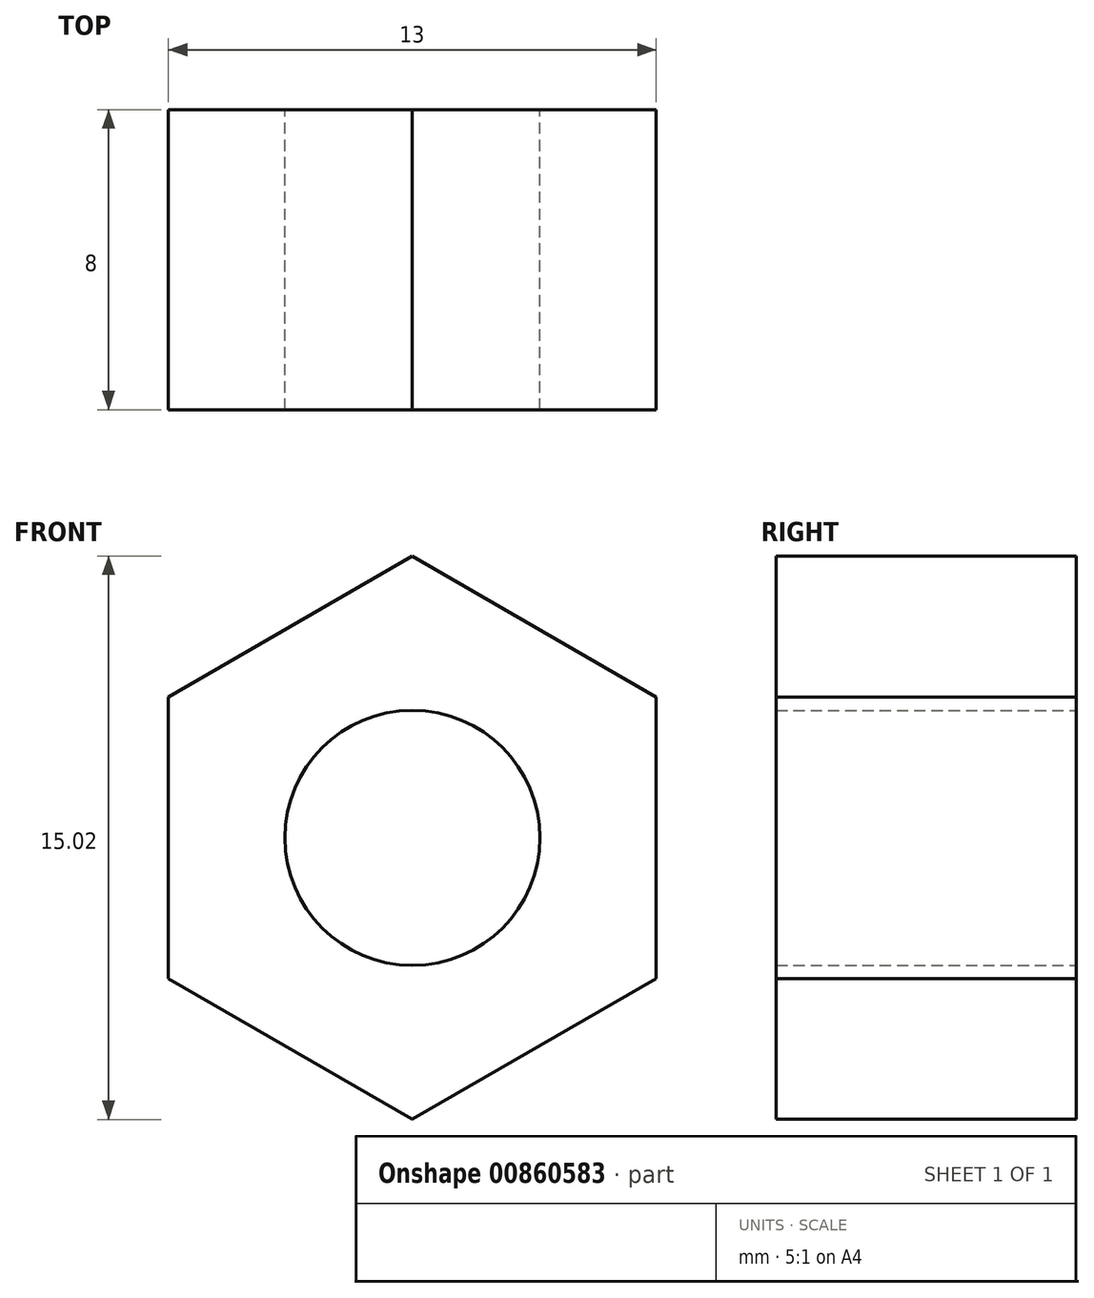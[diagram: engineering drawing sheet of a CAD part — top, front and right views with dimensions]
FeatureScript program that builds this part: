
annotation { "Feature Type Name" : "Feature", "Feature Type Description" : "" }
export const myFeature = defineFeature(function(context is Context, id is Id, definition is map)
    precondition{}
    {
        {
            var Q0;
            Q0=qCreatedBy(makeId("Front.planeOp"),FACE);
            var sketch = newSketch(context, id + "F0", { "sketchPlane" : qUnion([Q0])});
            skCircle(sketch, "E0.cCircle", {"center": v(0, 0) * mm, "radius": 6.5 * mm, "construction": true});
            skLineSegment(sketch, "E0.0", {"start": v(0, 7.5) * mm, "end": v(6.5, 3.75) * mm});
            skLineSegment(sketch, "E0.1", {"start": v(6.5, 3.75) * mm, "end": v(6.5, -3.75) * mm});
            skLineSegment(sketch, "E0.2", {"start": v(6.5, -3.75) * mm, "end": v(0, -7.5) * mm});
            skLineSegment(sketch, "E0.3", {"start": v(0, -7.5) * mm, "end": v(-6.5, -3.75) * mm});
            skLineSegment(sketch, "E0.4", {"start": v(-6.5, -3.75) * mm, "end": v(-6.5, 3.75) * mm});
            skLineSegment(sketch, "E0.5", {"start": v(-6.5, 3.75) * mm, "end": v(0, 7.5) * mm});
            skPoint(sketch, "E0.0.midPoint", {"position": v(3.25, 5.63) * mm});
            skCircle(sketch, "E1", {"center": v(0, 0) * mm, "radius": 3.4 * mm});
            skSolve(sketch);
        }
        {
            var Q0;
            Q0 = qSketchRegion(id + "F0", true);
            extrude(context, id + "F1", {"entities" : qUnion([Q0]), "depth" : 8 * mm, "offsetDistance" : 25 * mm});
        }
    });
